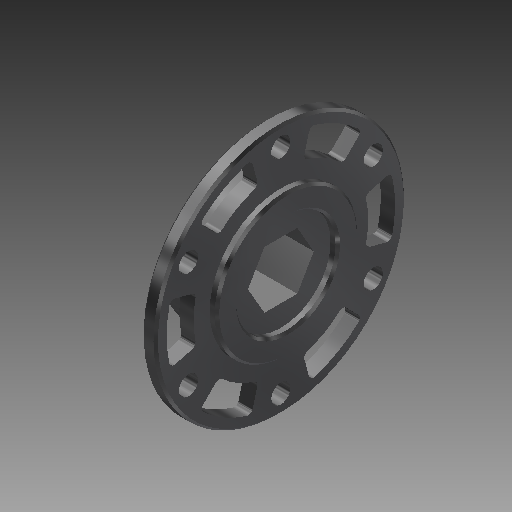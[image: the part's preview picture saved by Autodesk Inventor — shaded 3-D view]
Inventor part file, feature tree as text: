
AUTODESK INVENTOR PART (.ipt)
format: ipt  version: 2019 (Build 230136000, 136)  size: 274,944 bytes
history: native  units: in
note: dims shown in document units (in); Inventor stores cm internally (conversion verified against a paired STEP export)
features: imported_body x2, sketch x2, extrude x1, hole x1, pattern_circular x1
ambient origin geometry x8: Origin, YZ Plane, XZ Plane, XY Plane, X Axis, Y Axis, Z Axis, Center Point
bodies: Body1 (feature_tree)
feature tree (7):
  imported_body  "Imported1"
  extrude  "Extrusion1"  Depth=0.9375in
  hole  "Hole1"  [1 undecoded]
  pattern_circular  "Circular Pattern1"  [2 undecoded]
  imported_body  "Base1"
  sketch  "Sketch1"  dims[d0=1.0in d1=0.0in d2=0.9375in]
  sketch  "Sketch2"  dims[d3=0.169in d4=0.75in d5=0.375in d6=0.25in d7=0.5635in d8=1.0in d9=0.8108in d10=2.3622in d11=360.0deg]
note: 3 required parameter values undecoded (feature->parameter linkage not recoverable at this tier; creation-order binding heuristic only, values carry confidence <= 0.55)
